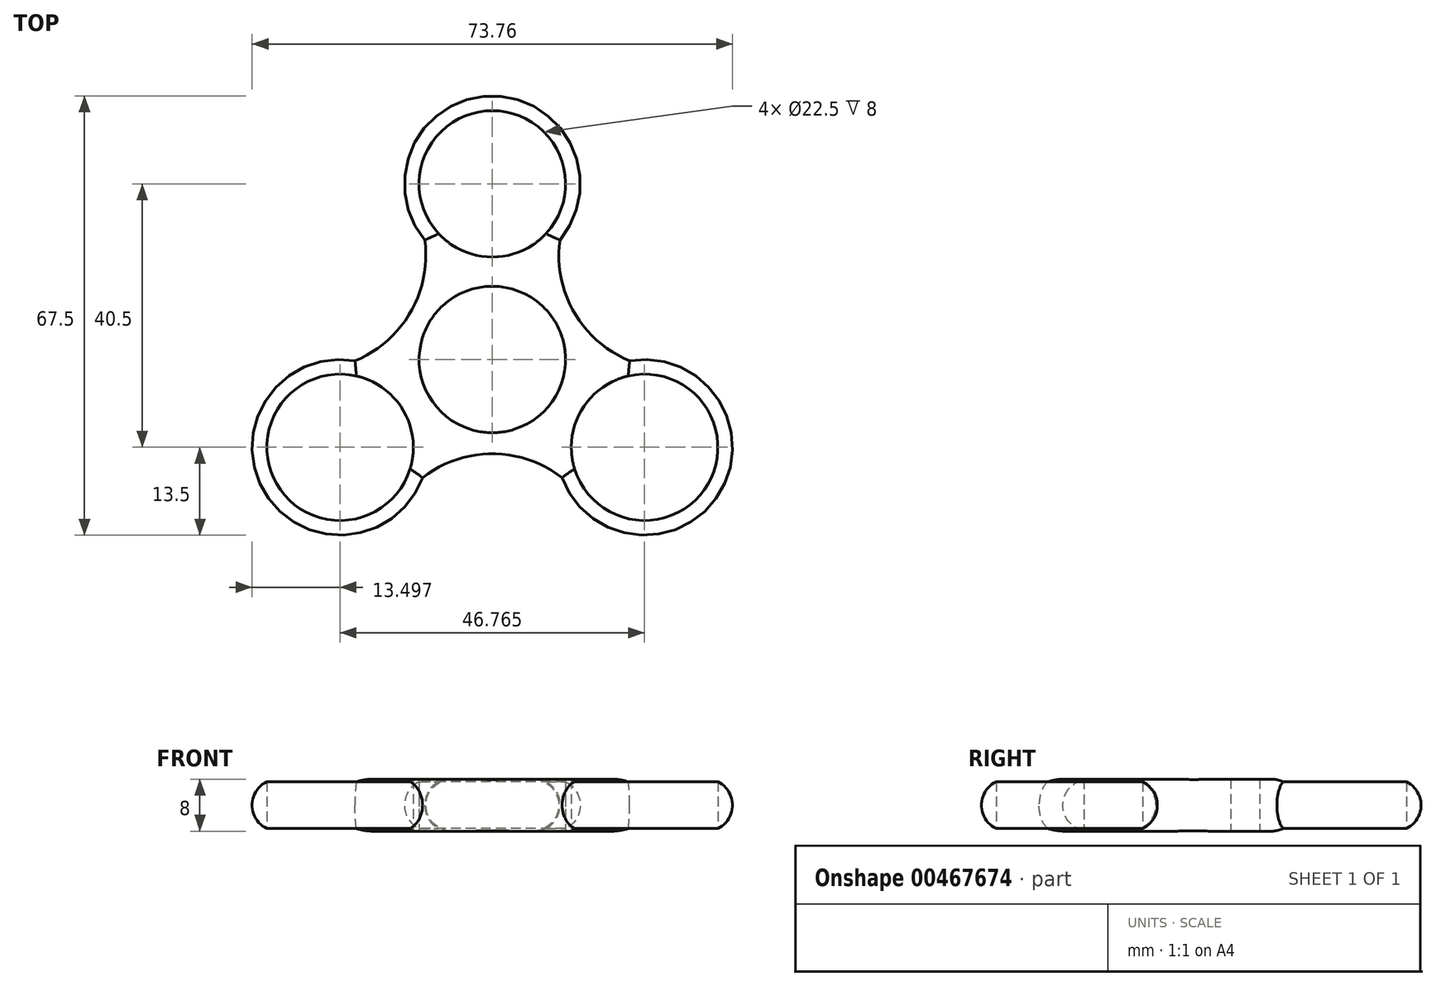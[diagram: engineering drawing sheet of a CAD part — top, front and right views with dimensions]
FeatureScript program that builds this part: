
annotation { "Feature Type Name" : "Feature", "Feature Type Description" : "" }
export const myFeature = defineFeature(function(context is Context, id is Id, definition is map)
    precondition{}
    {
        {
            var Q0;
            Q0=qCreatedBy(makeId("Top.planeOp"),FACE);
            var sketch = newSketch(context, id + "F0", { "sketchPlane" : qUnion([Q0])});
            skCircle(sketch, "E0", {"center": v(0, 0) * mm, "radius": 13.5 * mm});
            skCircle(sketch, "E1", {"center": v(0, 27) * mm, "radius": 13.5 * mm});
            skCircle(sketch, "E2", {"center": v(-23.38, -13.5) * mm, "radius": 13.5 * mm});
            skCircle(sketch, "E3", {"center": v(23.38, -13.5) * mm, "radius": 13.5 * mm});
            skLineSegment(sketch, "E4", {"start": v(-23.38, -13.5) * mm, "end": v(0, 0) * mm});
            skLineSegment(sketch, "E5", {"start": v(0, 0) * mm, "end": v(0, 27) * mm});
            skLineSegment(sketch, "E6", {"start": v(0, 0) * mm, "end": v(23.38, -13.5) * mm});
            skCircle(sketch, "E7", {"center": v(-23.38, -13.5) * mm, "radius": 11.25 * mm});
            skCircle(sketch, "E8", {"center": v(0, 27) * mm, "radius": 11.25 * mm});
            skCircle(sketch, "E9", {"center": v(23.38, -13.5) * mm, "radius": 11.25 * mm});
            skCircle(sketch, "E10", {"center": v(0, 0) * mm, "radius": 11.25 * mm});
            skPoint(sketch, "E11.2.internal.snap0", {"position": v(0, -17.54) * mm});
            skCircle(sketch, "E12", {"center": v(0, -32) * mm, "radius": 17.5 * mm});
            skLineSegment(sketch, "E13", {"start": v(0, 0) * mm, "end": v(0, -32) * mm});
            skLineSegment(sketch, "E14", {"start": v(0, 0) * mm, "end": v(37.54, 21.67) * mm});
            skLineSegment(sketch, "E15", {"start": v(0, 0) * mm, "end": v(-35.9, 20.73) * mm});
            skCircle(sketch, "E16", {"center": v(27.71, 16) * mm, "radius": 17.5 * mm});
            skCircle(sketch, "E17", {"center": v(-27.71, 16) * mm, "radius": 17.5 * mm});
            skSolve(sketch);
        }
        {
            var Q0;
            Q0=makeQuery(id+"F0.imprint","IMPRINT",FACE,{"disambiguationData":[TD([[makeQuery(id+"F0.imprint","IMPRINT",EDGE,{"derivedFrom":sQuery(id+"F0.wireOp",EDGE,"E7")}),-1.0]])]});
            var Q1;
            {var subQ0=sQuery(id+"F0.wireOp",EDGE,"E13");var subQ5=sQuery(id+"F0.wireOp",EDGE,"E12");var subQ6=makeQuery(id+"F0.imprint","INTERSECT",VERTEX,{"derivedFrom":[subQ5,subQ0]});Q1=makeQuery(id+"F0.imprint","IMPRINT",FACE,{"disambiguationData":[TD([[makeQuery(id+"F0.imprint","IMPRINT",EDGE,{"disambiguationData":[TD([[subQ6,-1.0]])],"derivedFrom":subQ5}),-1.0]])]});}
            var Q2;
            {var subQ0=sQuery(id+"F0.wireOp",EDGE,"E13");var subQ5=sQuery(id+"F0.wireOp",EDGE,"E12");var subQ7=makeQuery(id+"F0.imprint","INTERSECT",VERTEX,{"derivedFrom":[subQ5,subQ0]});Q2=makeQuery(id+"F0.imprint","IMPRINT",FACE,{"disambiguationData":[TD([[makeQuery(id+"F0.imprint","IMPRINT",EDGE,{"disambiguationData":[TD([[subQ7,1.0]])],"derivedFrom":subQ5}),-1.0]])]});}
            var Q3;
            Q3=makeQuery(id+"F0.imprint","IMPRINT",FACE,{"disambiguationData":[TD([[makeQuery(id+"F0.imprint","IMPRINT",EDGE,{"derivedFrom":sQuery(id+"F0.wireOp",EDGE,"E9")}),-1.0]])]});
            var Q4;
            Q4=makeQuery(id+"F0.imprint","IMPRINT",FACE,{"disambiguationData":[TD([[makeQuery(id+"F0.imprint","IMPRINT",EDGE,{"derivedFrom":sQuery(id+"F0.wireOp",EDGE,"E8")}),-1.0]])]});
            var Q5;
            {var subQ0=sQuery(id+"F0.wireOp",EDGE,"E15");var subQ5=sQuery(id+"F0.wireOp",EDGE,"E17");var subQ7=makeQuery(id+"F0.imprint","INTERSECT",VERTEX,{"derivedFrom":[subQ0,subQ5]});Q5=makeQuery(id+"F0.imprint","IMPRINT",FACE,{"disambiguationData":[TD([[makeQuery(id+"F0.imprint","IMPRINT",EDGE,{"disambiguationData":[TD([[subQ7,1.0]])],"derivedFrom":subQ0}),-1.0]])]});}
            var Q6;
            {var subQ0=sQuery(id+"F0.wireOp",EDGE,"E15");var subQ5=sQuery(id+"F0.wireOp",EDGE,"E17");var subQ7=makeQuery(id+"F0.imprint","INTERSECT",VERTEX,{"derivedFrom":[subQ0,subQ5]});Q6=makeQuery(id+"F0.imprint","IMPRINT",FACE,{"disambiguationData":[TD([[makeQuery(id+"F0.imprint","IMPRINT",EDGE,{"disambiguationData":[TD([[subQ7,1.0]])],"derivedFrom":subQ0}),1.0]])]});}
            var Q7;
            {var subQ0=sQuery(id+"F0.wireOp",EDGE,"E14");var subQ5=sQuery(id+"F0.wireOp",EDGE,"E16");var subQ7=makeQuery(id+"F0.imprint","INTERSECT",VERTEX,{"derivedFrom":[subQ0,subQ5]});Q7=makeQuery(id+"F0.imprint","IMPRINT",FACE,{"disambiguationData":[TD([[makeQuery(id+"F0.imprint","IMPRINT",EDGE,{"disambiguationData":[TD([[subQ7,1.0]])],"derivedFrom":subQ0}),1.0]])]});}
            var Q8;
            {var subQ0=sQuery(id+"F0.wireOp",EDGE,"E14");var subQ5=sQuery(id+"F0.wireOp",EDGE,"E16");var subQ7=makeQuery(id+"F0.imprint","INTERSECT",VERTEX,{"derivedFrom":[subQ0,subQ5]});Q8=makeQuery(id+"F0.imprint","IMPRINT",FACE,{"disambiguationData":[TD([[makeQuery(id+"F0.imprint","IMPRINT",EDGE,{"disambiguationData":[TD([[subQ7,1.0]])],"derivedFrom":subQ0}),-1.0]])]});}
            var Q9;
            {var subQ3=sQuery(id+"F0.wireOp",EDGE,"E6");var subQ5=sQuery(id+"F0.wireOp",EDGE,"E10");var subQ6=makeQuery(id+"F0.imprint","INTERSECT",VERTEX,{"derivedFrom":[subQ3,subQ5]});Q9=makeQuery(id+"F0.imprint","IMPRINT",FACE,{"disambiguationData":[TD([[makeQuery(id+"F0.imprint","IMPRINT",EDGE,{"disambiguationData":[TD([[subQ6,-1.0]])],"derivedFrom":subQ5}),-1.0]])]});}
            var Q10;
            {var subQ3=sQuery(id+"F0.wireOp",EDGE,"E6");var subQ5=sQuery(id+"F0.wireOp",EDGE,"E10");var subQ6=makeQuery(id+"F0.imprint","INTERSECT",VERTEX,{"derivedFrom":[subQ3,subQ5]});Q10=makeQuery(id+"F0.imprint","IMPRINT",FACE,{"disambiguationData":[TD([[makeQuery(id+"F0.imprint","IMPRINT",EDGE,{"disambiguationData":[TD([[subQ6,1.0]])],"derivedFrom":subQ5}),-1.0]])]});}
            var Q11;
            {var subQ3=sQuery(id+"F0.wireOp",EDGE,"E4");var subQ5=sQuery(id+"F0.wireOp",EDGE,"E10");var subQ6=makeQuery(id+"F0.imprint","INTERSECT",VERTEX,{"derivedFrom":[subQ3,subQ5]});Q11=makeQuery(id+"F0.imprint","IMPRINT",FACE,{"disambiguationData":[TD([[makeQuery(id+"F0.imprint","IMPRINT",EDGE,{"disambiguationData":[TD([[subQ6,-1.0]])],"derivedFrom":subQ5}),-1.0]])]});}
            var Q12;
            {var subQ3=sQuery(id+"F0.wireOp",EDGE,"E4");var subQ5=sQuery(id+"F0.wireOp",EDGE,"E10");var subQ6=makeQuery(id+"F0.imprint","INTERSECT",VERTEX,{"derivedFrom":[subQ3,subQ5]});Q12=makeQuery(id+"F0.imprint","IMPRINT",FACE,{"disambiguationData":[TD([[makeQuery(id+"F0.imprint","IMPRINT",EDGE,{"disambiguationData":[TD([[subQ6,1.0]])],"derivedFrom":subQ5}),-1.0]])]});}
            var Q13;
            {var subQ3=sQuery(id+"F0.wireOp",EDGE,"E5");var subQ5=sQuery(id+"F0.wireOp",EDGE,"E10");var subQ6=makeQuery(id+"F0.imprint","INTERSECT",VERTEX,{"derivedFrom":[subQ3,subQ5]});Q13=makeQuery(id+"F0.imprint","IMPRINT",FACE,{"disambiguationData":[TD([[makeQuery(id+"F0.imprint","IMPRINT",EDGE,{"disambiguationData":[TD([[subQ6,-1.0]])],"derivedFrom":subQ5}),-1.0]])]});}
            var Q14;
            {var subQ3=sQuery(id+"F0.wireOp",EDGE,"E5");var subQ5=sQuery(id+"F0.wireOp",EDGE,"E10");var subQ6=makeQuery(id+"F0.imprint","INTERSECT",VERTEX,{"derivedFrom":[subQ3,subQ5]});Q14=makeQuery(id+"F0.imprint","IMPRINT",FACE,{"disambiguationData":[TD([[makeQuery(id+"F0.imprint","IMPRINT",EDGE,{"disambiguationData":[TD([[subQ6,1.0]])],"derivedFrom":subQ5}),-1.0]])]});}
            var Q15;
            {var subQ0=sQuery(id+"F0.wireOp",EDGE,"E16");var subQ1=sQuery(id+"F0.wireOp",EDGE,"E3");var subQ2=makeQuery(id+"F0.imprint","INTERSECT",VERTEX,{"disambiguationData":[OD(0.0)],"derivedFrom":[subQ1,subQ0]});Q15=makeQuery(id+"F0.imprint","IMPRINT",FACE,{"disambiguationData":[TD([[makeQuery(id+"F0.imprint","IMPRINT",EDGE,{"disambiguationData":[TD([[subQ2,-1.0]])],"derivedFrom":subQ1}),1.0]])]});}
            var Q16;
            {var subQ0=sQuery(id+"F0.wireOp",EDGE,"E17");var subQ1=sQuery(id+"F0.wireOp",EDGE,"E2");var subQ2=makeQuery(id+"F0.imprint","INTERSECT",VERTEX,{"disambiguationData":[OD(0.0)],"derivedFrom":[subQ1,subQ0]});Q16=makeQuery(id+"F0.imprint","IMPRINT",FACE,{"disambiguationData":[TD([[makeQuery(id+"F0.imprint","IMPRINT",EDGE,{"disambiguationData":[TD([[subQ2,1.0]])],"derivedFrom":subQ1}),1.0]])]});}
            var Q17;
            {var subQ0=sQuery(id+"F0.wireOp",EDGE,"E12");var subQ1=sQuery(id+"F0.wireOp",EDGE,"E2");var subQ2=makeQuery(id+"F0.imprint","INTERSECT",VERTEX,{"disambiguationData":[OD(0.0)],"derivedFrom":[subQ1,subQ0]});Q17=makeQuery(id+"F0.imprint","IMPRINT",FACE,{"disambiguationData":[TD([[makeQuery(id+"F0.imprint","IMPRINT",EDGE,{"disambiguationData":[TD([[subQ2,-1.0]])],"derivedFrom":subQ1}),1.0]])]});}
            var Q18;
            {var subQ0=sQuery(id+"F0.wireOp",EDGE,"E12");var subQ1=sQuery(id+"F0.wireOp",EDGE,"E3");var subQ2=makeQuery(id+"F0.imprint","INTERSECT",VERTEX,{"disambiguationData":[OD(0.0)],"derivedFrom":[subQ1,subQ0]});Q18=makeQuery(id+"F0.imprint","IMPRINT",FACE,{"disambiguationData":[TD([[makeQuery(id+"F0.imprint","IMPRINT",EDGE,{"disambiguationData":[TD([[subQ2,1.0]])],"derivedFrom":subQ1}),1.0]])]});}
            var Q19;
            {var subQ0=sQuery(id+"F0.wireOp",EDGE,"E17");var subQ1=sQuery(id+"F0.wireOp",EDGE,"E1");var subQ2=makeQuery(id+"F0.imprint","INTERSECT",VERTEX,{"disambiguationData":[OD(0.0)],"derivedFrom":[subQ1,subQ0]});Q19=makeQuery(id+"F0.imprint","IMPRINT",FACE,{"disambiguationData":[TD([[makeQuery(id+"F0.imprint","IMPRINT",EDGE,{"disambiguationData":[TD([[subQ2,-1.0]])],"derivedFrom":subQ1}),1.0]])]});}
            var Q20;
            {var subQ0=sQuery(id+"F0.wireOp",EDGE,"E16");var subQ1=sQuery(id+"F0.wireOp",EDGE,"E1");var subQ2=makeQuery(id+"F0.imprint","INTERSECT",VERTEX,{"disambiguationData":[OD(0.0)],"derivedFrom":[subQ1,subQ0]});Q20=makeQuery(id+"F0.imprint","IMPRINT",FACE,{"disambiguationData":[TD([[makeQuery(id+"F0.imprint","IMPRINT",EDGE,{"disambiguationData":[TD([[subQ2,1.0]])],"derivedFrom":subQ1}),1.0]])]});}
            var Q21;
            {var subQ0=sQuery(id+"F0.wireOp",EDGE,"E17");var subQ1=sQuery(id+"F0.wireOp",EDGE,"E0");var subQ2=makeQuery(id+"F0.imprint","INTERSECT",VERTEX,{"disambiguationData":[OD(1.0)],"derivedFrom":[subQ1,subQ0]});Q21=makeQuery(id+"F0.imprint","IMPRINT",FACE,{"disambiguationData":[TD([[makeQuery(id+"F0.imprint","IMPRINT",EDGE,{"disambiguationData":[TD([[subQ2,1.0]])],"derivedFrom":subQ0}),-1.0]])]});}
            var Q22;
            {var subQ0=sQuery(id+"F0.wireOp",EDGE,"E12");var subQ1=sQuery(id+"F0.wireOp",EDGE,"E0");var subQ2=makeQuery(id+"F0.imprint","INTERSECT",VERTEX,{"disambiguationData":[OD(0.0)],"derivedFrom":[subQ1,subQ0]});Q22=makeQuery(id+"F0.imprint","IMPRINT",FACE,{"disambiguationData":[TD([[makeQuery(id+"F0.imprint","IMPRINT",EDGE,{"disambiguationData":[TD([[subQ2,-1.0]])],"derivedFrom":subQ0}),-1.0]])]});}
            var Q23;
            {var subQ0=sQuery(id+"F0.wireOp",EDGE,"E12");var subQ1=sQuery(id+"F0.wireOp",EDGE,"E0");var subQ2=makeQuery(id+"F0.imprint","INTERSECT",VERTEX,{"disambiguationData":[OD(1.0)],"derivedFrom":[subQ1,subQ0]});Q23=makeQuery(id+"F0.imprint","IMPRINT",FACE,{"disambiguationData":[TD([[makeQuery(id+"F0.imprint","IMPRINT",EDGE,{"disambiguationData":[TD([[subQ2,1.0]])],"derivedFrom":subQ0}),-1.0]])]});}
            var Q24;
            {var subQ0=sQuery(id+"F0.wireOp",EDGE,"E16");var subQ1=sQuery(id+"F0.wireOp",EDGE,"E0");var subQ2=makeQuery(id+"F0.imprint","INTERSECT",VERTEX,{"disambiguationData":[OD(0.0)],"derivedFrom":[subQ1,subQ0]});Q24=makeQuery(id+"F0.imprint","IMPRINT",FACE,{"disambiguationData":[TD([[makeQuery(id+"F0.imprint","IMPRINT",EDGE,{"disambiguationData":[TD([[subQ2,-1.0]])],"derivedFrom":subQ0}),-1.0]])]});}
            var Q25;
            {var subQ0=sQuery(id+"F0.wireOp",EDGE,"E17");var subQ1=sQuery(id+"F0.wireOp",EDGE,"E0");var subQ2=makeQuery(id+"F0.imprint","INTERSECT",VERTEX,{"disambiguationData":[OD(0.0)],"derivedFrom":[subQ1,subQ0]});Q25=makeQuery(id+"F0.imprint","IMPRINT",FACE,{"disambiguationData":[TD([[makeQuery(id+"F0.imprint","IMPRINT",EDGE,{"disambiguationData":[TD([[subQ2,-1.0]])],"derivedFrom":subQ0}),-1.0]])]});}
            var Q26;
            {var subQ0=sQuery(id+"F0.wireOp",EDGE,"E16");var subQ1=sQuery(id+"F0.wireOp",EDGE,"E0");var subQ2=makeQuery(id+"F0.imprint","INTERSECT",VERTEX,{"disambiguationData":[OD(1.0)],"derivedFrom":[subQ1,subQ0]});Q26=makeQuery(id+"F0.imprint","IMPRINT",FACE,{"disambiguationData":[TD([[makeQuery(id+"F0.imprint","IMPRINT",EDGE,{"disambiguationData":[TD([[subQ2,1.0]])],"derivedFrom":subQ0}),-1.0]])]});}
            extrude(context, id + "F1", {"entities" : qUnion([Q0, Q1, Q2, Q3, Q4, Q5, Q6, Q7, Q8, Q9, Q10, Q11, Q12, Q13, Q14, Q15, Q16, Q17, Q18, Q19, Q20, Q21, Q22, Q23, Q24, Q25, Q26]), "depth" : 8 * mm});
        }
        {
            var Q0;
            Q0=makeQuery(id+"F1.opExtrude","CAP_EDGE",EDGE,{"disambiguationData":[OSD([sQuery(id+"F0.wireOp",EDGE,"E16")])],"isStart":false});
            var Q1;
            Q1=makeQuery(id+"F1.opExtrude","CAP_EDGE",EDGE,{"disambiguationData":[OSD([sQuery(id+"F0.wireOp",EDGE,"E1")])],"isStart":false});
            var Q2;
            Q2=makeQuery(id+"F1.opExtrude","CAP_EDGE",EDGE,{"disambiguationData":[OSD([sQuery(id+"F0.wireOp",EDGE,"E17")])],"isStart":false});
            var Q3;
            Q3=makeQuery(id+"F1.opExtrude","CAP_EDGE",EDGE,{"disambiguationData":[OSD([sQuery(id+"F0.wireOp",EDGE,"E2")])],"isStart":false});
            var Q4;
            Q4=makeQuery(id+"F1.opExtrude","CAP_EDGE",EDGE,{"disambiguationData":[OSD([sQuery(id+"F0.wireOp",EDGE,"E12")])],"isStart":false});
            var Q5;
            Q5=makeQuery(id+"F1.opExtrude","CAP_EDGE",EDGE,{"disambiguationData":[OSD([sQuery(id+"F0.wireOp",EDGE,"E3")])],"isStart":false});
            var Q6;
            Q6=makeQuery(id+"F1.opExtrude","CAP_EDGE",EDGE,{"disambiguationData":[OSD([sQuery(id+"F0.wireOp",EDGE,"E1")])],"isStart":true});
            var Q7;
            Q7=makeQuery(id+"F1.opExtrude","CAP_EDGE",EDGE,{"disambiguationData":[OSD([sQuery(id+"F0.wireOp",EDGE,"E16")])],"isStart":true});
            var Q8;
            Q8=makeQuery(id+"F1.opExtrude","CAP_EDGE",EDGE,{"disambiguationData":[OSD([sQuery(id+"F0.wireOp",EDGE,"E3")])],"isStart":true});
            var Q9;
            Q9=makeQuery(id+"F1.opExtrude","CAP_EDGE",EDGE,{"disambiguationData":[OSD([sQuery(id+"F0.wireOp",EDGE,"E12")])],"isStart":true});
            var Q10;
            Q10=makeQuery(id+"F1.opExtrude","CAP_EDGE",EDGE,{"disambiguationData":[OSD([sQuery(id+"F0.wireOp",EDGE,"E2")])],"isStart":true});
            var Q11;
            Q11=makeQuery(id+"F1.opExtrude","CAP_EDGE",EDGE,{"disambiguationData":[OSD([sQuery(id+"F0.wireOp",EDGE,"E17")])],"isStart":true});
            fillet(context, id + "F2", {"entities" : qUnion([Q0, Q1, Q2, Q3, Q4, Q5, Q6, Q7, Q8, Q9, Q10, Q11]), "radius" : 4 * mm, "tangentPropagation" : true, "allowEdgeOverflow" : false});
        }
    });
